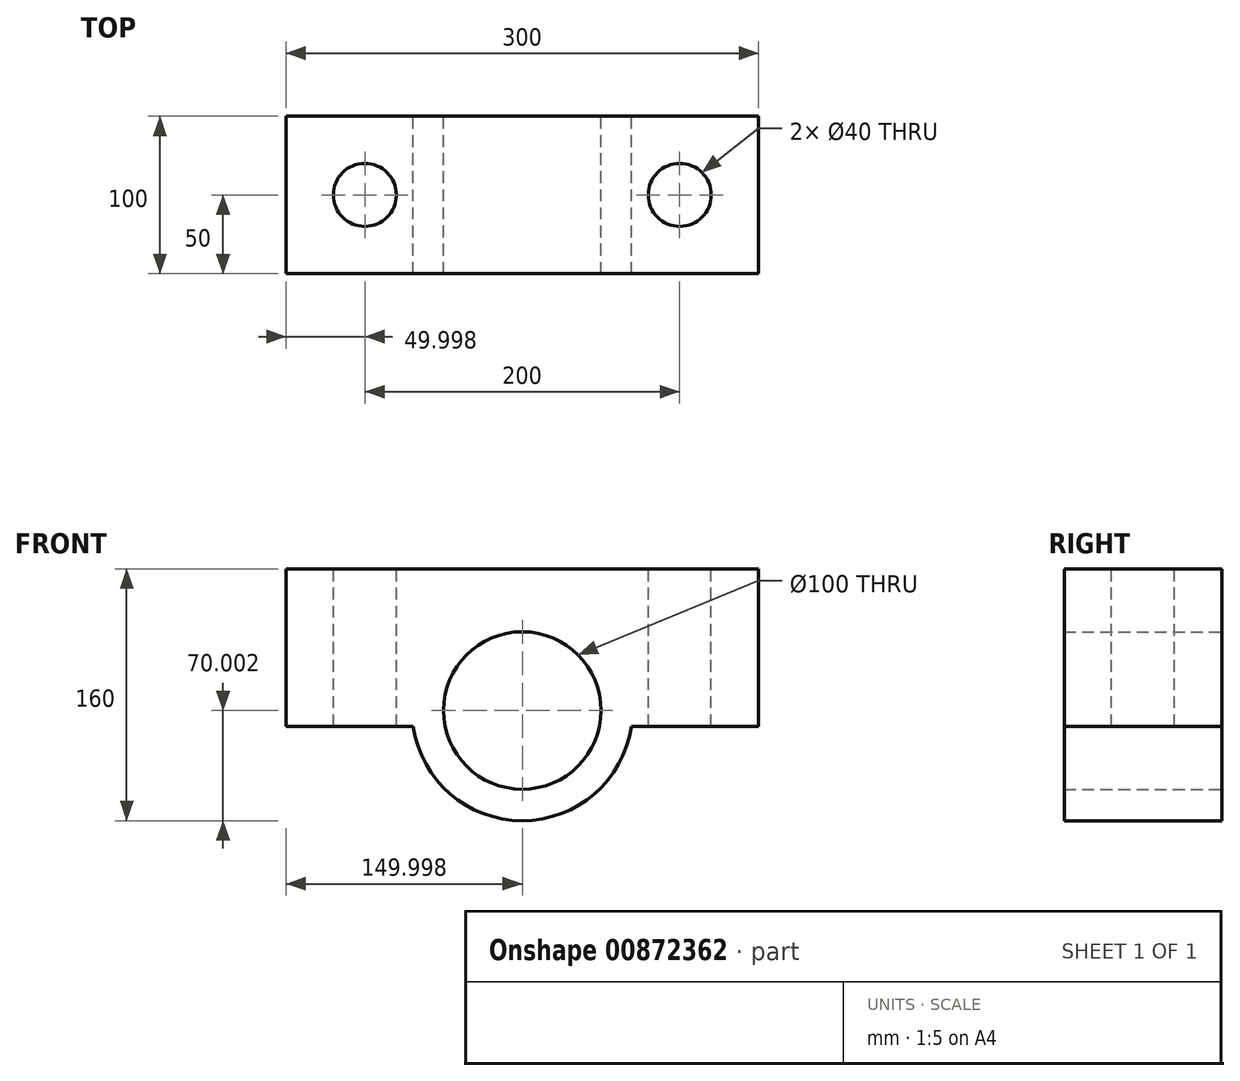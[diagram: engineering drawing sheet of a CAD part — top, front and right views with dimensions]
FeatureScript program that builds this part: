
annotation { "Feature Type Name" : "Feature", "Feature Type Description" : "" }
export const myFeature = defineFeature(function(context is Context, id is Id, definition is map)
    precondition{}
    {
        {
            var Q0;
            Q0=qCreatedBy(makeId("Front.planeOp"),FACE);
            var sketch = newSketch(context, id + "F0", { "sketchPlane" : qUnion([Q0])});
            skLineSegment(sketch, "E0.bottom", {"start": v(-148.34, 56.57) * mm, "end": v(151.66, 56.57) * mm});
            skLineSegment(sketch, "E0.top", {"start": v(-148.34, -43.43) * mm, "end": v(-67.62, -43.43) * mm});
            skLineSegment(sketch, "E0.left", {"start": v(-148.34, 56.57) * mm, "end": v(-148.34, -43.43) * mm});
            skLineSegment(sketch, "E0.right", {"start": v(151.66, 56.57) * mm, "end": v(151.66, -43.43) * mm});
            skPoint(sketch, "E1", {"position": v(1.66, -43.43) * mm});
            skCircle(sketch, "E2", {"center": v(1.66, -33.43) * mm, "radius": 50 * mm});
            skArc(sketch, "E3", {"start": v(-67.62, -43.43) * mm, "mid": v(1.66, -103.43) * mm, "end": v(70.94, -43.43) * mm});
            skLineSegment(sketch, "E4.trimOffspring", {"start": v(70.94, -43.43) * mm, "end": v(151.66, -43.43) * mm});
            skLineSegment(sketch, "E5.trimOffspring", {"start": v(-47.33, -43.43) * mm, "end": v(50.65, -43.43) * mm});
            skSolve(sketch);
        }
        {
            var Q0;
            Q0=makeQuery(id+"F0.imprint","IMPRINT",FACE,{"disambiguationData":[TD([[makeQuery(id+"F0.imprint","IMPRINT",EDGE,{"derivedFrom":sQuery(id+"F0.wireOp",EDGE,"E0.bottom")}),-1.0]])]});
            extrude(context, id + "F1", {"entities" : qUnion([Q0]), "depth" : 100 * mm, "offsetDistance" : 25 * mm});
        }
        {
            var Q0;
            Q0=makeQuery(id+"F1.opExtrude","SWEPT_FACE",FACE,{"disambiguationData":[OSD([sQuery(id+"F0.wireOp",EDGE,"E0.bottom")])]});
            var sketch = newSketch(context, id + "F2", { "sketchPlane" : qUnion([Q0])});
            skPoint(sketch, "E6", {"position": v(-98.34, -50) * mm});
            skPoint(sketch, "E7", {"position": v(101.66, -50) * mm});
            skSolve(sketch);
        }
        {
            var Q0;
            Q0=sQuery(id+"F2.wireOp",VERTEX,"E6");
            var Q1;
            Q1=sQuery(id+"F2.wireOp",VERTEX,"E7");
            var Q2;
            Q2=makeQuery(id+"F1.opExtrude","SWEPT_BODY",BODY,{"disambiguationData":[OSD([sQuery(id+"F0.wireOp",EDGE,"E0.bottom"),sQuery(id+"F0.wireOp",EDGE,"E0.top"),sQuery(id+"F0.wireOp",EDGE,"E0.left"),sQuery(id+"F0.wireOp",EDGE,"E0.right"),sQuery(id+"F0.wireOp",EDGE,"E2"),sQuery(id+"F0.wireOp",EDGE,"E3"),sQuery(id+"F0.wireOp",EDGE,"E4.trimOffspring")])]});
            hole(context, id + "F3", {"style" : HoleStyle.SIMPLE, "endStyle" : HoleEndStyle.THROUGH, "holeDiameter" : 40 * mm, "majorDiameter" : 5 * mm, "isTappedThrough" : true, "tappedDepth" : 12 * mm, "tapClearance" : 3, "locations" : qUnion([Q0, Q1]), "scope" : qUnion([Q2])});
        }
    });
